# Revit family: 5770 Minima Round IP65 Fire-Rated
name_source: partatom
category: Lighting Fixtures
revit_build: Autodesk Revit 2018 (Build: 20170223_1515(x64)
units: mm (PartAtom-declared; Revit-internal decimal feet)

## family parameters
Always vertical = Yes
Cut with Voids When Loaded = No
Host = Ceiling
Light Source = No
OmniClass Number = 23.80.70.11
OmniClass Title = Luminaries for Internal Lighting
Part Type = Normal
Room Calculation Point = No
Round Connector Dimension = Use Diameter
Shared = No

## types (2) — shared parameters

## per-type parameters (varying)
| type | Dimmable | Dimming Method | Driver Included | Driver Required | Efficacy (lm/w) | Electrical Class | Lamp | Light Source Fixed | Location Rating | Main Finish | Main Material | Power (Watts) | Product Location | Product Name |
| CE | Yes | Lamp Dependent | Not Applicable | No | Lamp Dependent | 2 | LED GU10 | Yes | IP65 | Various | Metal - Aluminium | 6W LED | Bathroom | Minima IP65 |
| ETL |  |  |  |  |  |  |  |  |  |  |  |  |  |  |

## geometry (parser evidence)
native form markers: Sweep x2
no freeform markers — native parametric forms only
